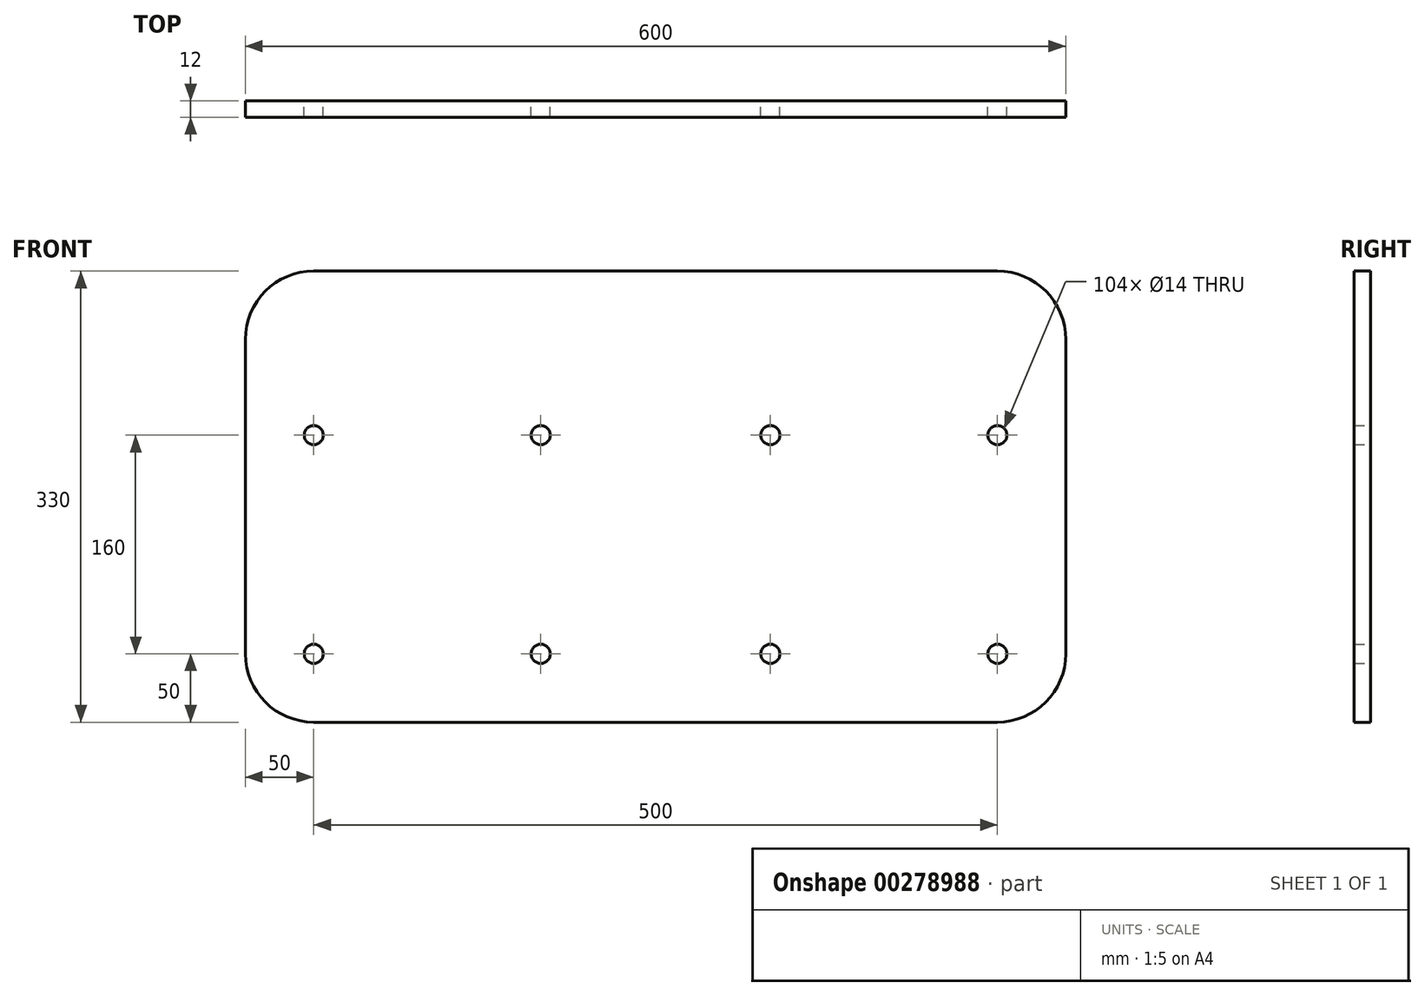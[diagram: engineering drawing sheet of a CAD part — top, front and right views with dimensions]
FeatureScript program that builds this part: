
annotation { "Feature Type Name" : "Feature", "Feature Type Description" : "" }
export const myFeature = defineFeature(function(context is Context, id is Id, definition is map)
    precondition{}
    {
        {
            var Q0;
            Q0=qCreatedBy(makeId("Front.planeOp"),FACE);
            var sketch = newSketch(context, id + "F0", { "sketchPlane" : qUnion([Q0])});
            skLineSegment(sketch, "E0.bottom", {"start": v(50, 0) * mm, "end": v(550, 0) * mm});
            skLineSegment(sketch, "E0.top", {"start": v(50, 330) * mm, "end": v(550, 330) * mm});
            skLineSegment(sketch, "E0.left", {"start": v(0, 50) * mm, "end": v(0, 280) * mm});
            skLineSegment(sketch, "E0.right", {"start": v(600, 50) * mm, "end": v(600, 280) * mm});
            skPoint(sketch, "E1.visualSharp", {"position": v(0, 330) * mm});
            skArc(sketch, "E1.filletArc", {"start": v(50, 330) * mm, "mid": v(14.64, 315.36) * mm, "end": v(0, 280) * mm});
            skPoint(sketch, "E2.visualSharp", {"position": v(600, 330) * mm});
            skArc(sketch, "E2.filletArc", {"start": v(600, 280) * mm, "mid": v(585.36, 315.36) * mm, "end": v(550, 330) * mm});
            skPoint(sketch, "E3.visualSharp", {"position": v(600, 0) * mm});
            skArc(sketch, "E3.filletArc", {"start": v(550, 0) * mm, "mid": v(585.36, 14.64) * mm, "end": v(600, 50) * mm});
            skPoint(sketch, "E4.visualSharp", {"position": v(0, 0) * mm});
            skArc(sketch, "E4.filletArc", {"start": v(0, 50) * mm, "mid": v(14.64, 14.64) * mm, "end": v(50, 0) * mm});
            skCircle(sketch, "E5", {"center": v(50, 210) * mm, "radius": 7 * mm});
            skCircle(sketch, "E6", {"center": v(50, 50) * mm, "radius": 7 * mm});
            skCircle(sketch, "E7", {"center": v(216, 210) * mm, "radius": 7 * mm});
            skCircle(sketch, "E8", {"center": v(216, 50) * mm, "radius": 7 * mm});
            skCircle(sketch, "E9", {"center": v(384, 210) * mm, "radius": 7 * mm});
            skCircle(sketch, "E10", {"center": v(384, 50) * mm, "radius": 7 * mm});
            skCircle(sketch, "E11", {"center": v(550, 210) * mm, "radius": 7 * mm});
            skCircle(sketch, "E12", {"center": v(550, 50) * mm, "radius": 7 * mm});
            skSolve(sketch);
        }
        {
            var Q0;
            Q0=makeQuery(id+"F0.imprint","IMPRINT",FACE,{"disambiguationData":[TD([[makeQuery(id+"F0.imprint","IMPRINT",EDGE,{"derivedFrom":sQuery(id+"F0.wireOp",EDGE,"E0.bottom")}),1.0]])]});
            extrude(context, id + "F1", {"entities" : qUnion([Q0]), "depth" : 12 * mm});
        }
    });
